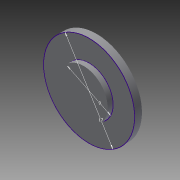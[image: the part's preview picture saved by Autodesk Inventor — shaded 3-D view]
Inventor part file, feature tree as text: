
AUTODESK INVENTOR PART (.ipt)
format: ipt  version: 2015 (Build 190159000, 159)  size: 79,360 bytes
history: native  units: mm
features: extrude x2, sketch x1
ambient origin geometry x8: Origin, YZ Plane, XZ Plane, XY Plane, X Axis, Y Axis, Z Axis, Center Point
bodies: Solid1 (feature_tree)
feature tree (3):
  sketch  "Sketch1"  dims[d0=17.0mm d1=9.0mm d2=1.4mm d3=0.0mm d4=1.0mm d5=0.0mm]
  extrude  "Extrusion1"  Depth=1.0mm
  extrude  "Extrusion2"  Depth=1.4mm TaperAngle=0.0deg
